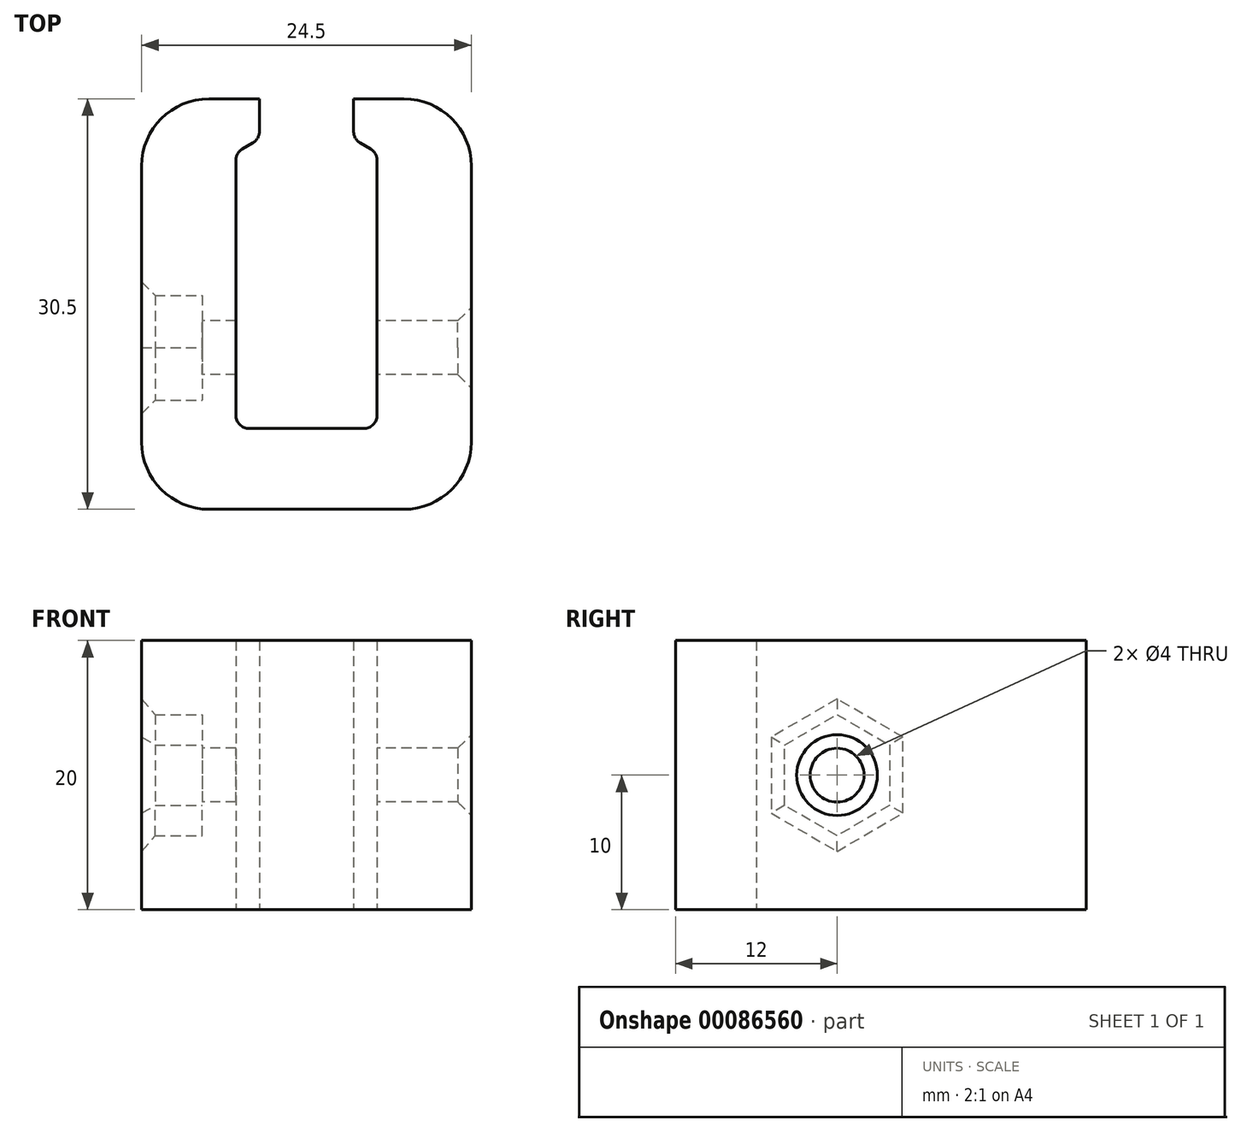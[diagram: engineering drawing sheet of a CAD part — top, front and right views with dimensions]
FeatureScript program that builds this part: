
annotation { "Feature Type Name" : "Feature", "Feature Type Description" : "" }
export const myFeature = defineFeature(function(context is Context, id is Id, definition is map)
    precondition{}
    {
        {
            var Q0;
            Q0=qCreatedBy(makeId("Top.planeOp"),FACE);
            var sketch = newSketch(context, id + "F0", { "sketchPlane" : qUnion([Q0])});
            skLineSegment(sketch, "E0.bottom", {"start": v(0, 0) * mm, "end": v(8.5, 0) * mm});
            skLineSegment(sketch, "E0.top", {"start": v(0, 14.5) * mm, "end": v(8.5, 14.5) * mm});
            skLineSegment(sketch, "E0.left", {"start": v(0, 0) * mm, "end": v(0, 14.5) * mm});
            skLineSegment(sketch, "E0.right", {"start": v(8.5, 0) * mm, "end": v(8.5, 14.5) * mm});
            skPoint(sketch, "E1", {"position": v(4.25, 0) * mm});
            skSolve(sketch);
        }
        {
            var Q0;
            Q0=qCreatedBy(makeId("Top.planeOp"),FACE);
            var sketch = newSketch(context, id + "F1", { "sketchPlane" : qUnion([Q0])});
            skLineSegment(sketch, "E2", {"start": v(-8, 14.5) * mm, "end": v(0.75, 14.5) * mm});
            skLineSegment(sketch, "E3", {"start": v(0.75, 14.5) * mm, "end": v(0.75, 11.5) * mm});
            skLineSegment(sketch, "E4", {"start": v(0.75, 11.5) * mm, "end": v(-1, 10.49) * mm});
            skLineSegment(sketch, "E5", {"start": v(-1, 10.49) * mm, "end": v(-1, -10) * mm});
            skLineSegment(sketch, "E6", {"start": v(-1, -10) * mm, "end": v(9.5, -10) * mm});
            skLineSegment(sketch, "E7", {"start": v(9.5, -10) * mm, "end": v(9.5, 10.49) * mm});
            skLineSegment(sketch, "E8", {"start": v(9.5, 10.49) * mm, "end": v(7.75, 11.5) * mm});
            skLineSegment(sketch, "E9", {"start": v(7.75, 11.5) * mm, "end": v(7.75, 14.5) * mm});
            skLineSegment(sketch, "E10", {"start": v(7.75, 14.5) * mm, "end": v(16.5, 14.5) * mm});
            skLineSegment(sketch, "E11", {"start": v(16.5, 14.5) * mm, "end": v(16.5, -16) * mm});
            skLineSegment(sketch, "E12", {"start": v(16.5, -16) * mm, "end": v(-8, -16) * mm});
            skLineSegment(sketch, "E13", {"start": v(-8, -16) * mm, "end": v(-8, 14.5) * mm});
            skPoint(sketch, "E14", {"position": v(4.25, -10) * mm});
            skSolve(sketch);
        }
        {
            var Q0;
            Q0=makeQuery(id+"F1.imprint","IMPRINT",FACE,{"disambiguationData":[TD([[makeQuery(id+"F1.imprint","IMPRINT",EDGE,{"derivedFrom":sQuery(id+"F1.wireOp",EDGE,"E2")}),-1.0]])]});
            var Q1;
            {var subQ3=sQuery(id+"F1.wireOp",EDGE,"EUQcXfTs-A3HZ-ymty-16cW-z9P9hBHx0nYE");Q1=makeQuery(id+"F1.imprint","IMPRINT",FACE,{"disambiguationData":[TD([[makeQuery(id+"F1.imprint","IMPRINT",EDGE,{"derivedFrom":subQ3}),-1.0]])]});}
            extrude(context, id + "F2", {"entities" : qUnion([Q0, Q1]), "depth" : 20 * mm});
        }
        {
            var Q0;
            Q0=makeQuery(id+"F2.opExtrude","SWEPT_EDGE",EDGE,{"disambiguationData":[OSD([sQuery(id+"F1.wireOp",EDGE,"E2"),sQuery(id+"F1.wireOp",EDGE,"E13")])]});
            var Q1;
            Q1=makeQuery(id+"F2.opExtrude","SWEPT_EDGE",EDGE,{"disambiguationData":[OSD([sQuery(id+"F1.wireOp",EDGE,"E10"),sQuery(id+"F1.wireOp",EDGE,"E11")])]});
            var Q2;
            Q2=makeQuery(id+"F2.opExtrude","SWEPT_EDGE",EDGE,{"disambiguationData":[OSD([sQuery(id+"F1.wireOp",EDGE,"E12"),sQuery(id+"F1.wireOp",EDGE,"E13")])]});
            var Q3;
            Q3=makeQuery(id+"F2.opExtrude","SWEPT_EDGE",EDGE,{"disambiguationData":[OSD([sQuery(id+"F1.wireOp",EDGE,"E11"),sQuery(id+"F1.wireOp",EDGE,"E12")])]});
            fillet(context, id + "F3", {"entities" : qUnion([Q0, Q1, Q2, Q3]), "radius" : 5 * mm, "tangentPropagation" : true, "allowEdgeOverflow" : false});
        }
        {
            var Q0;
            Q0=makeQuery(id+"F3.opFillet","BLEND_EDGE",EDGE,{"blendedFrom":[makeQuery(id+"F2.opExtrude","SWEPT_EDGE",EDGE,{"disambiguationData":[OSD([sQuery(id+"F1.wireOp",EDGE,"E2"),sQuery(id+"F1.wireOp",EDGE,"E13")])]}),makeQuery(id+"F2.opExtrude","SWEPT_FACE",FACE,{"disambiguationData":[OSD([sQuery(id+"F1.wireOp",EDGE,"E3")])]})],"blendedInto":[makeQuery(id+"F2.opExtrude","SWEPT_FACE",FACE,{"disambiguationData":[OSD([sQuery(id+"F1.wireOp",EDGE,"E3")])]})]});
            var Q1;
            Q1=makeQuery(id+"F2.opExtrude","SWEPT_EDGE",EDGE,{"disambiguationData":[OSD([sQuery(id+"F1.wireOp",EDGE,"E3"),sQuery(id+"F1.wireOp",EDGE,"E4")])]});
            var Q2;
            Q2=makeQuery(id+"F3.opFillet","BLEND_EDGE",EDGE,{"blendedFrom":[makeQuery(id+"F2.opExtrude","SWEPT_EDGE",EDGE,{"disambiguationData":[OSD([sQuery(id+"F1.wireOp",EDGE,"E10"),sQuery(id+"F1.wireOp",EDGE,"E11")])]}),makeQuery(id+"F2.opExtrude","SWEPT_FACE",FACE,{"disambiguationData":[OSD([sQuery(id+"F1.wireOp",EDGE,"E9")])]})],"blendedInto":[makeQuery(id+"F2.opExtrude","SWEPT_FACE",FACE,{"disambiguationData":[OSD([sQuery(id+"F1.wireOp",EDGE,"E9")])]})]});
            var Q3;
            Q3=makeQuery(id+"F2.opExtrude","SWEPT_EDGE",EDGE,{"disambiguationData":[OSD([sQuery(id+"F1.wireOp",EDGE,"E8"),sQuery(id+"F1.wireOp",EDGE,"E9")])]});
            var Q4;
            Q4=makeQuery(id+"F2.opExtrude","SWEPT_EDGE",EDGE,{"disambiguationData":[OSD([sQuery(id+"F1.wireOp",EDGE,"E4"),sQuery(id+"F1.wireOp",EDGE,"E5")])]});
            var Q5;
            Q5=makeQuery(id+"F2.opExtrude","SWEPT_EDGE",EDGE,{"disambiguationData":[OSD([sQuery(id+"F1.wireOp",EDGE,"E7"),sQuery(id+"F1.wireOp",EDGE,"E8")])]});
            var Q6;
            Q6=makeQuery(id+"F2.opExtrude","SWEPT_EDGE",EDGE,{"disambiguationData":[OSD([sQuery(id+"F1.wireOp",EDGE,"E5"),sQuery(id+"F1.wireOp",EDGE,"EUQcXfTs-A3HZ-ymty-16cW-z9P9hBHx0nYE")])]});
            var Q7;
            Q7=makeQuery(id+"F2.opExtrude","SWEPT_EDGE",EDGE,{"disambiguationData":[OSD([sQuery(id+"F1.wireOp",EDGE,"EUQcXfTs-A3HZ-ymty-16cW-z9P9hBHx0nYE"),sQuery(id+"F1.wireOp",EDGE,"uVDAqgWB-B6HG-cSPM-7tU5-nBvEZKKER4gJ")])]});
            var Q8;
            Q8=makeQuery(id+"F2.opExtrude","SWEPT_EDGE",EDGE,{"disambiguationData":[OSD([sQuery(id+"F1.wireOp",EDGE,"E6"),sQuery(id+"F1.wireOp",EDGE,"uVDAqgWB-B6HG-cSPM-7tU5-nBvEZKKER4gJ")])]});
            var Q9;
            Q9=makeQuery(id+"F2.opExtrude","SWEPT_EDGE",EDGE,{"disambiguationData":[OSD([sQuery(id+"F1.wireOp",EDGE,"E6"),sQuery(id+"F1.wireOp",EDGE,"E7")])]});
            fillet(context, id + "F4", {"entities" : qUnion([Q0, Q1, Q2, Q3, Q4, Q5, Q6, Q7, Q8, Q9]), "radius" : 1 * mm, "tangentPropagation" : true, "allowEdgeOverflow" : false});
        }
        {
            var Q0;
            Q0=makeQuery(id+"F2.opExtrude","SWEPT_FACE",FACE,{"disambiguationData":[OSD([sQuery(id+"F1.wireOp",EDGE,"E5")])]});
            var sketch = newSketch(context, id + "F5", { "sketchPlane" : qUnion([Q0])});
            skPoint(sketch, "E15", {"position": v(-4, 0) * mm});
            skCircle(sketch, "E16.cCircle", {"center": v(-4, 10) * mm, "radius": 4.5 * mm, "construction": true});
            skLineSegment(sketch, "E16.0", {"start": v(-4, 5.5) * mm, "end": v(-7.9, 7.75) * mm});
            skLineSegment(sketch, "E16.1", {"start": v(-7.9, 7.75) * mm, "end": v(-7.9, 12.25) * mm});
            skLineSegment(sketch, "E16.2", {"start": v(-7.9, 12.25) * mm, "end": v(-4, 14.5) * mm});
            skLineSegment(sketch, "E16.3", {"start": v(-4, 14.5) * mm, "end": v(-0.1, 12.25) * mm});
            skLineSegment(sketch, "E16.4", {"start": v(-0.1, 12.25) * mm, "end": v(-0.1, 7.75) * mm});
            skLineSegment(sketch, "E16.5", {"start": v(-0.1, 7.75) * mm, "end": v(-4, 5.5) * mm});
            skPoint(sketch, "E17", {"position": v(-9, 10) * mm});
            skSolve(sketch);
        }
        {
            var Q0;
            Q0 = qSketchRegion(id + "F5", true);
            extrude(context, id + "F6", {"entities" : qUnion([Q0]), "operationType" : NewBodyOperationType.REMOVE, "oppositeDirection" : true, "depth" : 10 * mm, "hasSecondDirection" : true, "secondDirectionOppositeDirection" : true, "secondDirectionDepth" : 2.5 * mm});
        }
        {
            var Q0;
            Q0=makeQuery(id+"F6.boolean.opBoolean","COPY",FACE,{"derivedFrom":makeQuery(id+"F6.opExtrude","CAP_FACE",FACE,{"disambiguationData":[OSD([sQuery(id+"F5.wireOp",EDGE,"E16.0"),sQuery(id+"F5.wireOp",EDGE,"E16.1"),sQuery(id+"F5.wireOp",EDGE,"E16.2"),sQuery(id+"F5.wireOp",EDGE,"E16.3"),sQuery(id+"F5.wireOp",EDGE,"E16.4"),sQuery(id+"F5.wireOp",EDGE,"E16.5")])],"isStart":true})});
            var sketch = newSketch(context, id + "F7", { "sketchPlane" : qUnion([Q0])});
            skCircle(sketch, "E18", {"center": v(4, 10) * mm, "radius": 2 * mm});
            skPoint(sketch, "E18.centerSnap0", {"position": v(0.1, 10) * mm});
            skSolve(sketch);
        }
        {
            var Q0;
            Q0=makeQuery(id+"F7.imprint","IMPRINT",FACE,{"disambiguationData":[TD([[makeQuery(id+"F7.imprint","IMPRINT",EDGE,{"derivedFrom":sQuery(id+"F7.wireOp",EDGE,"E18")}),1.0]])]});
            extrude(context, id + "F8", {"entities" : qUnion([Q0]), "operationType" : NewBodyOperationType.REMOVE, "oppositeDirection" : true, "depth" : 25 * mm});
        }
        {
            var Q0;
            Q0=makeQuery(id+"F6.boolean.opBoolean","INTERSECT",EDGE,{"derivedFrom":[makeQuery(id+"F2.opExtrude","SWEPT_FACE",FACE,{"disambiguationData":[OSD([sQuery(id+"F1.wireOp",EDGE,"E13")])]}),makeQuery(id+"F6.opExtrude","SWEPT_FACE",FACE,{"disambiguationData":[OSD([sQuery(id+"F5.wireOp",EDGE,"E16.1")])]})]});
            var Q1;
            Q1=makeQuery(id+"F6.boolean.opBoolean","INTERSECT",EDGE,{"derivedFrom":[makeQuery(id+"F2.opExtrude","SWEPT_FACE",FACE,{"disambiguationData":[OSD([sQuery(id+"F1.wireOp",EDGE,"E13")])]}),makeQuery(id+"F6.opExtrude","SWEPT_FACE",FACE,{"disambiguationData":[OSD([sQuery(id+"F5.wireOp",EDGE,"E16.2")])]})]});
            var Q2;
            Q2=makeQuery(id+"F6.boolean.opBoolean","INTERSECT",EDGE,{"derivedFrom":[makeQuery(id+"F2.opExtrude","SWEPT_FACE",FACE,{"disambiguationData":[OSD([sQuery(id+"F1.wireOp",EDGE,"E13")])]}),makeQuery(id+"F6.opExtrude","SWEPT_FACE",FACE,{"disambiguationData":[OSD([sQuery(id+"F5.wireOp",EDGE,"E16.3")])]})]});
            var Q3;
            Q3=makeQuery(id+"F6.boolean.opBoolean","INTERSECT",EDGE,{"derivedFrom":[makeQuery(id+"F2.opExtrude","SWEPT_FACE",FACE,{"disambiguationData":[OSD([sQuery(id+"F1.wireOp",EDGE,"E13")])]}),makeQuery(id+"F6.opExtrude","SWEPT_FACE",FACE,{"disambiguationData":[OSD([sQuery(id+"F5.wireOp",EDGE,"E16.4")])]})]});
            var Q4;
            Q4=makeQuery(id+"F6.boolean.opBoolean","INTERSECT",EDGE,{"derivedFrom":[makeQuery(id+"F2.opExtrude","SWEPT_FACE",FACE,{"disambiguationData":[OSD([sQuery(id+"F1.wireOp",EDGE,"E13")])]}),makeQuery(id+"F6.opExtrude","SWEPT_FACE",FACE,{"disambiguationData":[OSD([sQuery(id+"F5.wireOp",EDGE,"E16.0")])]})]});
            var Q5;
            Q5=makeQuery(id+"F6.boolean.opBoolean","INTERSECT",EDGE,{"derivedFrom":[makeQuery(id+"F2.opExtrude","SWEPT_FACE",FACE,{"disambiguationData":[OSD([sQuery(id+"F1.wireOp",EDGE,"E13")])]}),makeQuery(id+"F6.opExtrude","SWEPT_FACE",FACE,{"disambiguationData":[OSD([sQuery(id+"F5.wireOp",EDGE,"E16.5")])]})]});
            chamfer(context, id + "F9", {"entities" : qUnion([Q0, Q1, Q2, Q3, Q4, Q5]), "width" : 1 * mm, "tangentPropagation" : true});
        }
        {
            var Q0;
            Q0=makeQuery(id+"F8.boolean.opBoolean","INTERSECT",EDGE,{"derivedFrom":[makeQuery(id+"F2.opExtrude","SWEPT_FACE",FACE,{"disambiguationData":[OSD([sQuery(id+"F1.wireOp",EDGE,"uVDAqgWB-B6HG-cSPM-7tU5-nBvEZKKER4gJ")])]}),makeQuery(id+"F8.opExtrude","SWEPT_FACE",FACE,{"disambiguationData":[OSD([sQuery(id+"F7.wireOp",EDGE,"E18")])]})]});
            var Q1;
            Q1=makeQuery(id+"F8.boolean.opBoolean","INTERSECT",EDGE,{"derivedFrom":[makeQuery(id+"F2.opExtrude","SWEPT_FACE",FACE,{"disambiguationData":[OSD([sQuery(id+"F1.wireOp",EDGE,"E11")])]}),makeQuery(id+"F8.opExtrude","SWEPT_FACE",FACE,{"disambiguationData":[OSD([sQuery(id+"F7.wireOp",EDGE,"E18")])]})]});
            chamfer(context, id + "F10", {"entities" : qUnion([Q0, Q1]), "width" : 1 * mm, "tangentPropagation" : true});
        }
    });
